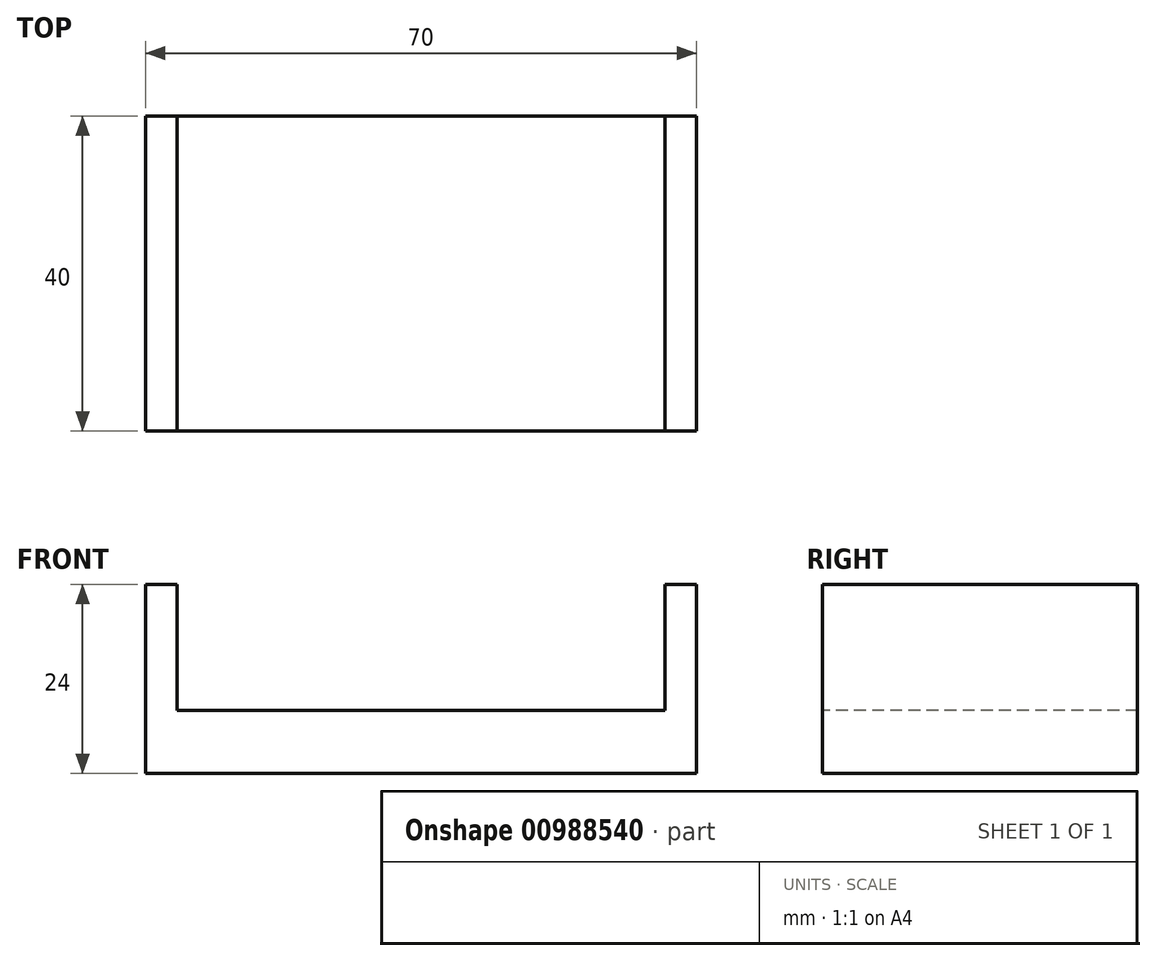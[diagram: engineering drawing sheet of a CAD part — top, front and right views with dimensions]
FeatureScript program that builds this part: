
annotation { "Feature Type Name" : "Feature", "Feature Type Description" : "" }
export const myFeature = defineFeature(function(context is Context, id is Id, definition is map)
    precondition{}
    {
        {
            var Q0;
            Q0=qCreatedBy(makeId("Top.planeOp"),FACE);
            var sketch = newSketch(context, id + "F0", { "sketchPlane" : qUnion([Q0])});
            skLineSegment(sketch, "E0.bottom", {"start": v(-33, 20) * mm, "end": v(33, 20) * mm});
            skLineSegment(sketch, "E0.top", {"start": v(-33, -20) * mm, "end": v(33, -20) * mm});
            skLineSegment(sketch, "E0.left", {"start": v(-33, 20) * mm, "end": v(-33, -20) * mm});
            skLineSegment(sketch, "E0.right", {"start": v(33, 20) * mm, "end": v(33, -20) * mm});
            skPoint(sketch, "E0.middle", {"position": v(0, 0) * mm});
            skSolve(sketch);
        }
        {
            var Q0;
            Q0=makeQuery(id+"F0.imprint","IMPRINT",FACE,{"disambiguationData":[TD([[makeQuery(id+"F0.imprint","IMPRINT",EDGE,{"derivedFrom":sQuery(id+"F0.wireOp",EDGE,"E0.bottom")}),-1.0]])]});
            extrude(context, id + "F1", {"entities" : qUnion([Q0]), "depth" : 2 * mm, "offsetDistance" : 25 * mm});
        }
        {
            var Q0;
            Q0=makeQuery(id+"F0.imprint","IMPRINT",FACE,{"disambiguationData":[TD([[makeQuery(id+"F0.imprint","IMPRINT",EDGE,{"derivedFrom":sQuery(id+"F0.wireOp",EDGE,"E0.bottom")}),-1.0]])]});
            extrude(context, id + "F2", {"entities" : qUnion([Q0]), "operationType" : NewBodyOperationType.ADD, "depth" : 2 * mm, "offsetDistance" : 25 * mm});
        }
        {
            var Q0;
            Q0=makeQuery(id+"F1.opExtrude","CAP_FACE",FACE,{"disambiguationData":[OSD([sQuery(id+"F0.wireOp",EDGE,"E0.bottom"),sQuery(id+"F0.wireOp",EDGE,"E0.top"),sQuery(id+"F0.wireOp",EDGE,"E0.left"),sQuery(id+"F0.wireOp",EDGE,"E0.right")])],"isStart":false});
            var sketch = newSketch(context, id + "F3", { "sketchPlane" : qUnion([Q0])});
            skLineSegment(sketch, "E1", {"start": v(-31, 20) * mm, "end": v(-31, -20) * mm});
            skLineSegment(sketch, "E2", {"start": v(31, 20) * mm, "end": v(31, -20) * mm});
            skSolve(sketch);
        }
        {
            var Q0;
            {var subQ0=sQuery(id+"F3.wireOp",EDGE,"E1");Q0=makeQuery(id+"F3.imprint","IMPRINT",FACE,{"disambiguationData":[TD([[makeQuery(id+"F3.imprint","IMPRINT",EDGE,{"derivedFrom":subQ0}),-1.0]])]});}
            var Q1;
            {var subQ0=sQuery(id+"F3.wireOp",EDGE,"E2");Q1=makeQuery(id+"F3.imprint","IMPRINT",FACE,{"disambiguationData":[TD([[makeQuery(id+"F3.imprint","IMPRINT",EDGE,{"derivedFrom":subQ0}),1.0]])]});}
            extrude(context, id + "F4", {"entities" : qUnion([Q0, Q1]), "operationType" : NewBodyOperationType.ADD, "depth" : 16 * mm, "offsetDistance" : 25 * mm});
        }
        {
            var Q0;
            {var subQ0=sQuery(id+"F0.wireOp",EDGE,"E0.right");Q0=makeQuery(id+"F4.boolean.opBoolean","MERGE",FACE,{"derivedFrom":[makeQuery(id+"F1.opExtrude","SWEPT_FACE",FACE,{"disambiguationData":[OSD([subQ0])]}),makeQuery(id+"F4.opExtrude","SWEPT_FACE",FACE,{"disambiguationData":[OSD([subQ0])]})]});}
            extrude(context, id + "F5", {"entities" : qUnion([Q0]), "operationType" : NewBodyOperationType.ADD, "depth" : 2 * mm, "offsetDistance" : 25 * mm});
        }
        {
            var Q0;
            {var subQ0=sQuery(id+"F0.wireOp",EDGE,"E0.left");Q0=makeQuery(id+"F4.boolean.opBoolean","MERGE",FACE,{"derivedFrom":[makeQuery(id+"F1.opExtrude","SWEPT_FACE",FACE,{"disambiguationData":[OSD([subQ0])]}),makeQuery(id+"F4.opExtrude","SWEPT_FACE",FACE,{"disambiguationData":[OSD([subQ0])]})]});}
            extrude(context, id + "F6", {"entities" : qUnion([Q0]), "operationType" : NewBodyOperationType.ADD, "depth" : 2 * mm, "offsetDistance" : 25 * mm});
        }
        {
            var Q0;
            {var subQ0=sQuery(id+"F0.wireOp",EDGE,"E0.left");var subQ1=sQuery(id+"F0.wireOp",EDGE,"E0.right");Q0=makeQuery(id+"F6.boolean.opBoolean","MERGE",FACE,{"derivedFrom":[makeQuery(id+"F5.boolean.opBoolean","MERGE",FACE,{"derivedFrom":[makeQuery(id+"F1.opExtrude","CAP_FACE",FACE,{"disambiguationData":[OSD([sQuery(id+"F0.wireOp",EDGE,"E0.bottom"),sQuery(id+"F0.wireOp",EDGE,"E0.top"),subQ0,subQ1])],"isStart":true}),makeQuery(id+"F5.opExtrude","SWEPT_FACE",FACE,{"disambiguationData":[OSD([subQ1]),TDD([makeQuery(id+"F1.opExtrude","CAP_EDGE",EDGE,{"disambiguationData":[OSD([subQ1])],"isStart":true})])]})]}),makeQuery(id+"F6.opExtrude","SWEPT_FACE",FACE,{"disambiguationData":[OSD([subQ0]),TDD([makeQuery(id+"F1.opExtrude","CAP_EDGE",EDGE,{"disambiguationData":[OSD([subQ0])],"isStart":true})])]})]});}
            extrude(context, id + "F7", {"entities" : qUnion([Q0]), "operationType" : NewBodyOperationType.ADD, "depth" : 4 * mm, "offsetDistance" : 25 * mm});
        }
        {
            var Q0;
            Q0=makeQuery(id+"F7.opExtrude","CAP_FACE",FACE,{"disambiguationData":[OSD([sQuery(id+"F0.wireOp",EDGE,"E0.bottom"),sQuery(id+"F0.wireOp",EDGE,"E0.top"),sQuery(id+"F0.wireOp",EDGE,"E0.left"),sQuery(id+"F0.wireOp",EDGE,"E0.right")])],"isStart":false});
            extrude(context, id + "F8", {"entities" : qUnion([Q0]), "operationType" : NewBodyOperationType.ADD, "depth" : 2 * mm, "offsetDistance" : 25 * mm});
        }
    });
